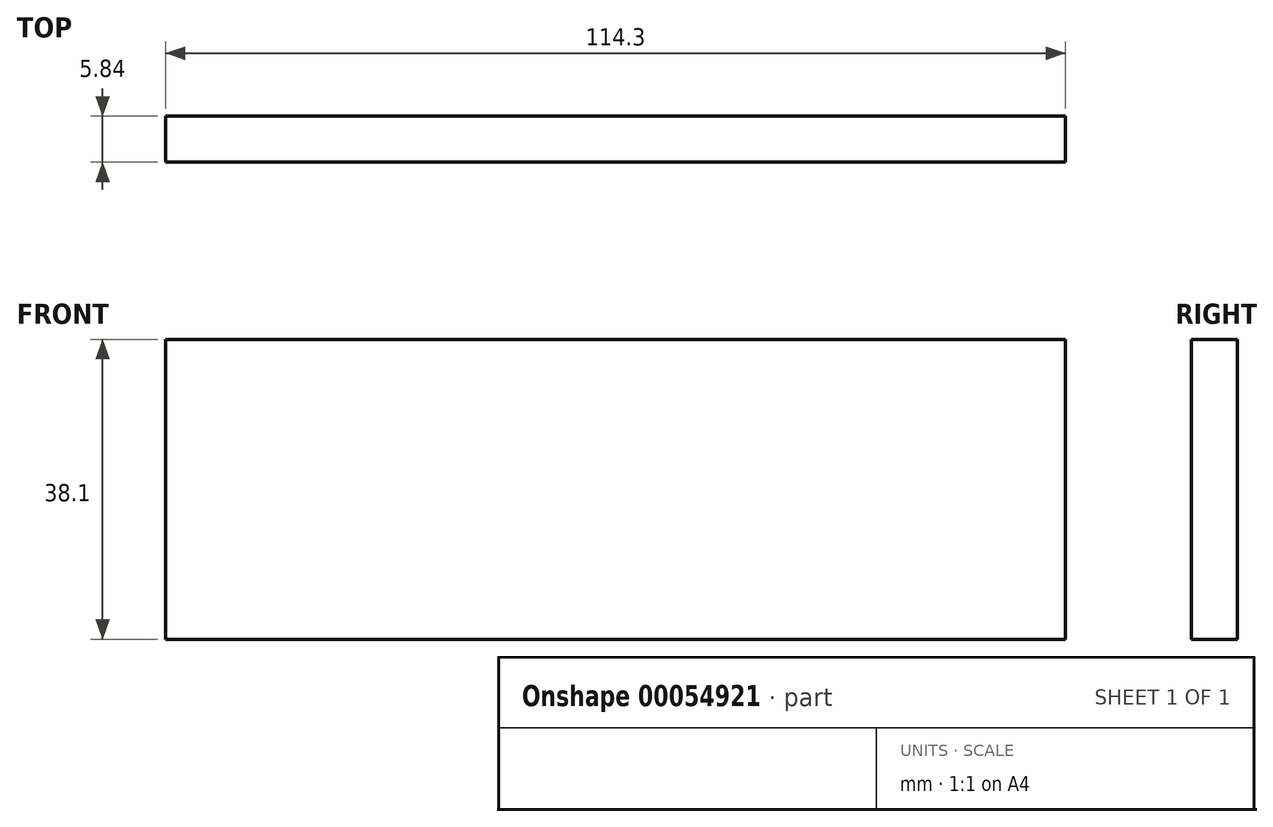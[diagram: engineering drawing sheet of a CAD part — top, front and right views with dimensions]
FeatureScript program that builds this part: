
annotation { "Feature Type Name" : "Feature", "Feature Type Description" : "" }
export const myFeature = defineFeature(function(context is Context, id is Id, definition is map)
    precondition{}
    {
        {
            var Q0;
            Q0=qCreatedBy(makeId("Front.planeOp"),FACE);
            var sketch = newSketch(context, id + "F0", { "sketchPlane" : qUnion([Q0])});
            skLineSegment(sketch, "E0.bottom", {"start": v(-87.98, -33.38) * mm, "end": v(26.32, -33.38) * mm});
            skLineSegment(sketch, "E0.top", {"start": v(-87.98, -71.48) * mm, "end": v(26.32, -71.48) * mm});
            skLineSegment(sketch, "E0.left", {"start": v(-87.98, -33.38) * mm, "end": v(-87.98, -71.48) * mm});
            skLineSegment(sketch, "E0.right", {"start": v(26.32, -33.38) * mm, "end": v(26.32, -71.48) * mm});
            skLineSegment(sketch, "E1.bottom", {"start": v(-56.23, -33.38) * mm, "end": v(-5.43, -33.38) * mm});
            skLineSegment(sketch, "E1.top", {"start": v(-56.23, -30.84) * mm, "end": v(-5.43, -30.84) * mm});
            skLineSegment(sketch, "E1.left", {"start": v(-56.23, -33.38) * mm, "end": v(-56.23, -30.84) * mm});
            skLineSegment(sketch, "E1.right", {"start": v(-5.43, -33.38) * mm, "end": v(-5.43, -30.84) * mm});
            skLineSegment(sketch, "E2.bottom", {"start": v(-56.23, -71.48) * mm, "end": v(-5.43, -71.48) * mm});
            skLineSegment(sketch, "E2.top", {"start": v(-56.23, -74.02) * mm, "end": v(-5.43, -74.02) * mm});
            skLineSegment(sketch, "E2.left", {"start": v(-56.23, -71.48) * mm, "end": v(-56.23, -74.02) * mm});
            skLineSegment(sketch, "E2.right", {"start": v(-5.43, -71.48) * mm, "end": v(-5.43, -74.02) * mm});
            skPoint(sketch, "E3", {"position": v(-30.83, -30.84) * mm});
            skPoint(sketch, "E4", {"position": v(-30.83, -74.02) * mm});
            skPoint(sketch, "E5", {"position": v(-30.83, -71.48) * mm});
            skLineSegment(sketch, "E6.bottom", {"start": v(-82.14, -33.38) * mm, "end": v(-69.44, -33.38) * mm});
            skLineSegment(sketch, "E6.top", {"start": v(-82.14, -30.84) * mm, "end": v(-69.44, -30.84) * mm});
            skLineSegment(sketch, "E6.left", {"start": v(-82.14, -33.38) * mm, "end": v(-82.14, -30.84) * mm});
            skLineSegment(sketch, "E6.right", {"start": v(-69.44, -33.38) * mm, "end": v(-69.44, -30.84) * mm});
            skLineSegment(sketch, "E7.bottom", {"start": v(20.48, -33.38) * mm, "end": v(7.78, -33.38) * mm});
            skLineSegment(sketch, "E7.top", {"start": v(20.48, -30.84) * mm, "end": v(7.78, -30.84) * mm});
            skLineSegment(sketch, "E7.left", {"start": v(20.48, -33.38) * mm, "end": v(20.48, -30.84) * mm});
            skLineSegment(sketch, "E7.right", {"start": v(7.78, -33.38) * mm, "end": v(7.78, -30.84) * mm});
            skLineSegment(sketch, "E8.bottom", {"start": v(-82.14, -71.48) * mm, "end": v(-69.44, -71.48) * mm});
            skLineSegment(sketch, "E8.top", {"start": v(-82.14, -74.02) * mm, "end": v(-69.44, -74.02) * mm});
            skLineSegment(sketch, "E8.left", {"start": v(-82.14, -71.48) * mm, "end": v(-82.14, -74.02) * mm});
            skLineSegment(sketch, "E8.right", {"start": v(-69.44, -71.48) * mm, "end": v(-69.44, -74.02) * mm});
            skLineSegment(sketch, "E9.bottom", {"start": v(20.48, -71.48) * mm, "end": v(7.78, -71.48) * mm});
            skLineSegment(sketch, "E9.top", {"start": v(20.48, -74.02) * mm, "end": v(7.78, -74.02) * mm});
            skLineSegment(sketch, "E9.left", {"start": v(20.48, -71.48) * mm, "end": v(20.48, -74.02) * mm});
            skLineSegment(sketch, "E9.right", {"start": v(7.78, -71.48) * mm, "end": v(7.78, -74.02) * mm});
            skSolve(sketch);
        }
        {
            var Q0;
            {var subQ3=sQuery(id+"F0.wireOp",EDGE,"E0.left");Q0=makeQuery(id+"F0.imprint","IMPRINT",FACE,{"disambiguationData":[TD([[makeQuery(id+"F0.imprint","IMPRINT",EDGE,{"derivedFrom":subQ3}),1.0]])]});}
            var Q1;
            Q1=makeQuery(id+"F0.imprint","IMPRINT",FACE,{"disambiguationData":[TD([[makeQuery(id+"F0.imprint","IMPRINT",EDGE,{"derivedFrom":sQuery(id+"F0.wireOp",EDGE,"E1.bottom")}),1.0]])]});
            var Q2;
            Q2=makeQuery(id+"F0.imprint","IMPRINT",FACE,{"disambiguationData":[TD([[makeQuery(id+"F0.imprint","IMPRINT",EDGE,{"derivedFrom":sQuery(id+"F0.wireOp",EDGE,"E2.bottom")}),-1.0]])]});
            var Q3;
            Q3=makeQuery(id+"F0.imprint","IMPRINT",FACE,{"disambiguationData":[TD([[makeQuery(id+"F0.imprint","IMPRINT",EDGE,{"derivedFrom":sQuery(id+"F0.wireOp",EDGE,"E6.bottom")}),1.0]])]});
            var Q4;
            Q4=makeQuery(id+"F0.imprint","IMPRINT",FACE,{"disambiguationData":[TD([[makeQuery(id+"F0.imprint","IMPRINT",EDGE,{"derivedFrom":sQuery(id+"F0.wireOp",EDGE,"E8.bottom")}),-1.0]])]});
            var Q5;
            Q5=makeQuery(id+"F0.imprint","IMPRINT",FACE,{"disambiguationData":[TD([[makeQuery(id+"F0.imprint","IMPRINT",EDGE,{"derivedFrom":sQuery(id+"F0.wireOp",EDGE,"E7.bottom")}),-1.0]])]});
            var Q6;
            Q6=makeQuery(id+"F0.imprint","IMPRINT",FACE,{"disambiguationData":[TD([[makeQuery(id+"F0.imprint","IMPRINT",EDGE,{"derivedFrom":sQuery(id+"F0.wireOp",EDGE,"E9.bottom")}),1.0]])]});
            extrude(context, id + "F1", {"entities" : qUnion([Q0, Q1, Q2, Q3, Q4, Q5, Q6]), "depth" : 5.84 * mm});
        }
    });
